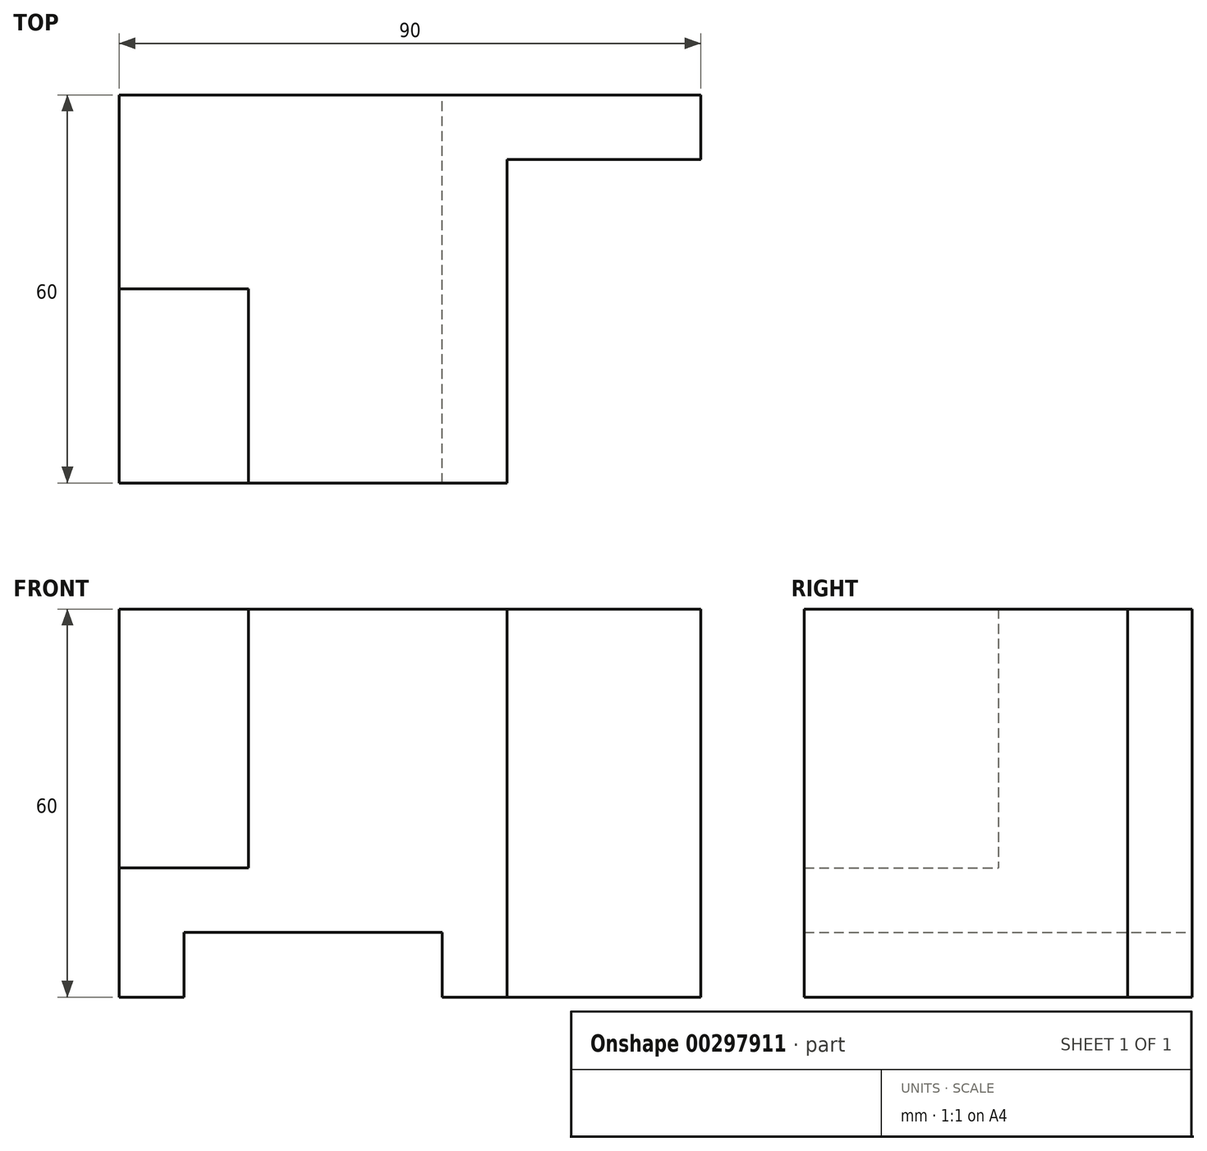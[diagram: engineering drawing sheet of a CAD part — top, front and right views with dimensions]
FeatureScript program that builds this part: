
annotation { "Feature Type Name" : "Feature", "Feature Type Description" : "" }
export const myFeature = defineFeature(function(context is Context, id is Id, definition is map)
    precondition{}
    {
        {
            var Q0;
            Q0=qCreatedBy(makeId("Front.planeOp"),FACE);
            var sketch = newSketch(context, id + "F0", { "sketchPlane" : qUnion([Q0])});
            skLineSegment(sketch, "E0.bottom", {"start": v(45, 30) * mm, "end": v(-45, 30) * mm});
            skLineSegment(sketch, "E0.top", {"start": v(45, -30) * mm, "end": v(-45, -30) * mm});
            skLineSegment(sketch, "E0.left", {"start": v(45, 30) * mm, "end": v(45, -30) * mm});
            skLineSegment(sketch, "E0.right", {"start": v(-45, 30) * mm, "end": v(-45, -30) * mm});
            skPoint(sketch, "E0.middle", {"position": v(0, 0) * mm});
            skLineSegment(sketch, "E1", {"start": v(15, 30) * mm, "end": v(15, -30) * mm});
            skLineSegment(sketch, "E2", {"start": v(5, -30) * mm, "end": v(5, -20) * mm});
            skLineSegment(sketch, "E3", {"start": v(5, -20) * mm, "end": v(-35, -20) * mm});
            skLineSegment(sketch, "E4", {"start": v(-35, -20) * mm, "end": v(-35, -30) * mm});
            skLineSegment(sketch, "E5", {"start": v(-25, 30) * mm, "end": v(-25, -10) * mm});
            skLineSegment(sketch, "E6", {"start": v(-25, -10) * mm, "end": v(-45, -10) * mm});
            skSolve(sketch);
        }
        {
            var Q0;
            {var subQ4=sQuery(id+"F0.wireOp",EDGE,"E1");Q0=makeQuery(id+"F0.imprint","IMPRINT",FACE,{"disambiguationData":[TD([[makeQuery(id+"F0.imprint","IMPRINT",EDGE,{"derivedFrom":subQ4}),-1.0]])]});}
            extrude(context, id + "F1", {"entities" : qUnion([Q0]), "depth" : 60 * mm});
        }
        {
            var Q0;
            {var subQ0=sQuery(id+"F0.wireOp",EDGE,"E0.left");Q0=makeQuery(id+"F0.imprint","IMPRINT",FACE,{"disambiguationData":[TD([[makeQuery(id+"F0.imprint","IMPRINT",EDGE,{"derivedFrom":subQ0}),-1.0]])]});}
            extrude(context, id + "F2", {"entities" : qUnion([Q0]), "operationType" : NewBodyOperationType.ADD, "depth" : 10 * mm});
        }
        {
            var Q0;
            {var subQ3=sQuery(id+"F0.wireOp",EDGE,"E5");Q0=makeQuery(id+"F0.imprint","IMPRINT",FACE,{"disambiguationData":[TD([[makeQuery(id+"F0.imprint","IMPRINT",EDGE,{"derivedFrom":subQ3}),-1.0]])]});}
            extrude(context, id + "F3", {"entities" : qUnion([Q0]), "operationType" : NewBodyOperationType.ADD, "depth" : 30 * mm});
        }
    });
